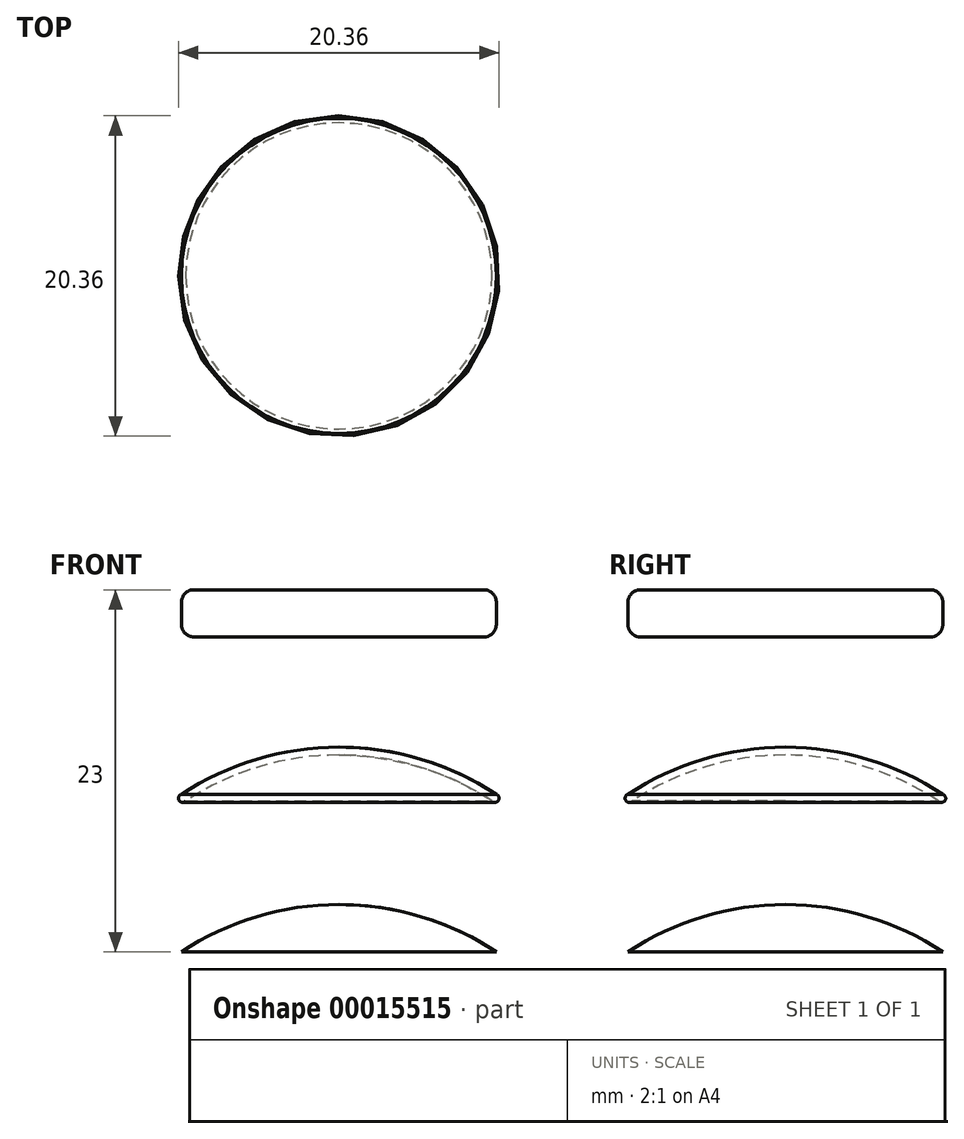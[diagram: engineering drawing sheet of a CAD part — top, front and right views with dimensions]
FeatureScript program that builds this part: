
annotation { "Feature Type Name" : "Feature", "Feature Type Description" : "" }
export const myFeature = defineFeature(function(context is Context, id is Id, definition is map)
    precondition{}
    {
        {
            var Q0;
            Q0=qCreatedBy(makeId("Front.planeOp"),FACE);
            var sketch = newSketch(context, id + "F0", { "sketchPlane" : qUnion([Q0])});
            skLineSegment(sketch, "E0", {"start": v(0, 0) * mm, "end": v(10, 0) * mm});
            skLineSegment(sketch, "E1", {"start": v(0, 0) * mm, "end": v(0, 3) * mm});
            skLineSegment(sketch, "E2", {"start": v(0, 3) * mm, "end": v(10, 3) * mm, "construction": true});
            skLineSegment(sketch, "E3", {"start": v(10, 3) * mm, "end": v(10, 0) * mm, "construction": true});
            skArc(sketch, "E4", {"start": v(10, 0) * mm, "mid": v(5.22, 2.23) * mm, "end": v(0, 3) * mm});
            skLineSegment(sketch, "E5.bottom", {"start": v(0, 20) * mm, "end": v(10, 20) * mm});
            skLineSegment(sketch, "E5.top", {"start": v(0, 23) * mm, "end": v(10, 23) * mm});
            skLineSegment(sketch, "E5.left", {"start": v(0, 20) * mm, "end": v(0, 23) * mm});
            skLineSegment(sketch, "E5.right", {"start": v(10, 20) * mm, "end": v(10, 23) * mm});
            skArc(sketch, "E6.0.1.0", {"start": v(10, 10) * mm, "mid": v(5.22, 12.23) * mm, "end": v(0, 13) * mm});
            skLineSegment(sketch, "E6.0.1.3", {"start": v(0, 12.5) * mm, "end": v(0, 13) * mm});
            skLineSegment(sketch, "E6.direction1", {"start": v(0, -15.17) * mm, "end": v(25, -15.17) * mm, "construction": true});
            skLineSegment(sketch, "E6.direction2", {"start": v(0, -5.17) * mm, "end": v(0, -15.17) * mm, "construction": true});
            skArc(sketch, "E7.0", {"start": v(9.72, 9.58) * mm, "mid": v(5.08, 11.75) * mm, "end": v(0, 12.5) * mm});
            skPoint(sketch, "E8.orphan", {"position": v(0, 10) * mm});
            skArc(sketch, "E9", {"start": v(9.72, 9.58) * mm, "mid": v(10.14, 9.6) * mm, "end": v(10, 10) * mm});
            skPoint(sketch, "E9.third.point", {"position": v(9.72, 9.92) * mm});
            skSolve(sketch);
        }
        {
            var Q0;
            Q0 = qSketchRegion(id + "F0", true);
            var Q1;
            Q1=sQuery(id+"F0.wireOp",EDGE,"E1");
            revolve(context, id + "F1", {"entities" : qUnion([Q0]), "axis" : qUnion([Q1]), "revolveType" : RevolveType.FULL});
        }
        {
            var Q0;
            Q0=makeQuery(id+"F1.opRevolve","SWEPT_EDGE",EDGE,{"disambiguationData":[OSD([sQuery(id+"F0.wireOp",EDGE,"E5.top"),sQuery(id+"F0.wireOp",EDGE,"E5.right")])]});
            var Q1;
            Q1=makeQuery(id+"F1.opRevolve","SWEPT_EDGE",EDGE,{"disambiguationData":[OSD([sQuery(id+"F0.wireOp",EDGE,"E5.bottom"),sQuery(id+"F0.wireOp",EDGE,"E5.right")])]});
            fillet(context, id + "F2", {"entities" : qUnion([Q0, Q1]), "radius" : 0.8 * mm, "tangentPropagation" : true, "allowEdgeOverflow" : false});
        }
    });
